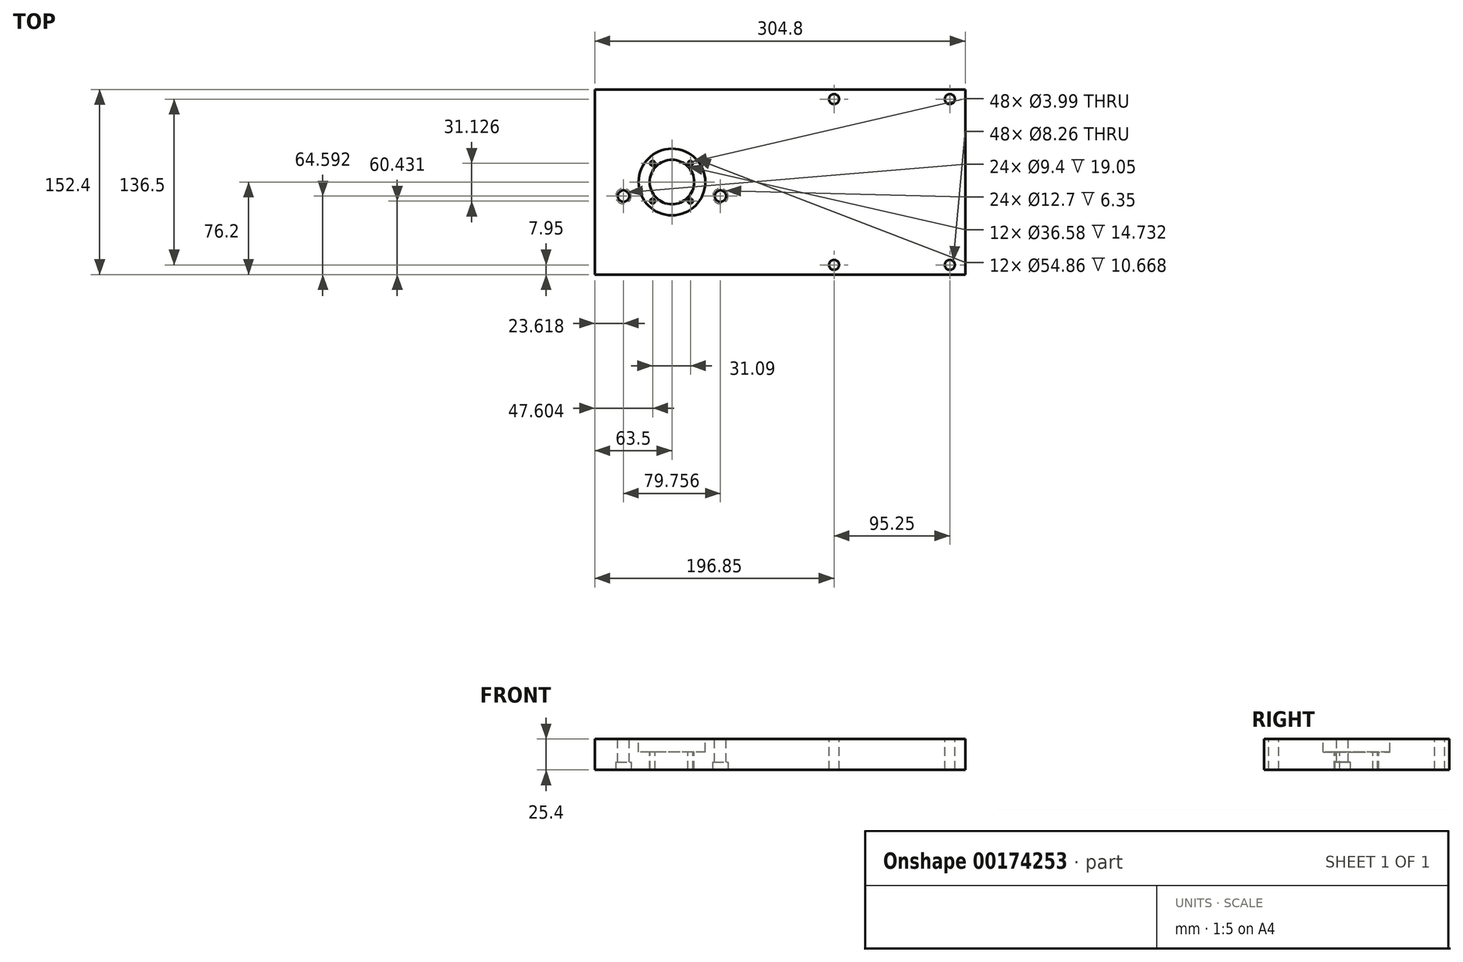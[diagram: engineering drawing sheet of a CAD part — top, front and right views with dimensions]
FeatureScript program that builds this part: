
annotation { "Feature Type Name" : "Feature", "Feature Type Description" : "" }
export const myFeature = defineFeature(function(context is Context, id is Id, definition is map)
    precondition{}
    {
        {
            var Q0;
            Q0=qCreatedBy(makeId("Top.planeOp"),FACE);
            var sketch = newSketch(context, id + "F0", { "sketchPlane" : qUnion([Q0])});
            skLineSegment(sketch, "E0.bottom", {"start": v(-152.4, 76.2) * mm, "end": v(152.4, 76.2) * mm});
            skLineSegment(sketch, "E0.top", {"start": v(-152.4, -76.2) * mm, "end": v(152.4, -76.2) * mm});
            skLineSegment(sketch, "E0.left", {"start": v(-152.4, 76.2) * mm, "end": v(-152.4, -76.2) * mm});
            skLineSegment(sketch, "E0.right", {"start": v(152.4, 76.2) * mm, "end": v(152.4, -76.2) * mm});
            skPoint(sketch, "E0.middle", {"position": v(0, 0) * mm});
            skSolve(sketch);
        }
        {
            var Q0;
            Q0=qSketchRegion(id+"F0",true);
            extrude(context, id + "F1", {"entities" : qUnion([Q0]), "oppositeDirection" : true, "depth" : 25.4 * mm});
        }
        {
            var Q0;
            Q0=makeQuery(id+"F1.opExtrude","CAP_FACE",FACE,{"disambiguationData":[OSD([sQuery(id+"F0.wireOp",EDGE,"E0.bottom"),sQuery(id+"F0.wireOp",EDGE,"E0.top"),sQuery(id+"F0.wireOp",EDGE,"E0.left"),sQuery(id+"F0.wireOp",EDGE,"E0.right")])],"isStart":true});
            var sketch = newSketch(context, id + "F2", { "sketchPlane" : qUnion([Q0])});
            skCircle(sketch, "E1", {"center": v(-88.9, 0) * mm, "radius": 18.29 * mm});
            skSolve(sketch);
        }
        {
            var Q0;
            Q0=qSketchRegion(id+"F2",true);
            extrude(context, id + "F3", {"entities" : qUnion([Q0]), "operationType" : NewBodyOperationType.REMOVE, "endBound" : BoundingType.THROUGH_ALL, "oppositeDirection" : true, "depth" : 25.4 * mm});
        }
        {
            var Q0;
            Q0=makeQuery(id+"F1.opExtrude","CAP_FACE",FACE,{"disambiguationData":[OSD([sQuery(id+"F0.wireOp",EDGE,"E0.bottom"),sQuery(id+"F0.wireOp",EDGE,"E0.top"),sQuery(id+"F0.wireOp",EDGE,"E0.left"),sQuery(id+"F0.wireOp",EDGE,"E0.right")])],"isStart":true});
            var sketch = newSketch(context, id + "F4", { "sketchPlane" : qUnion([Q0])});
            skCircle(sketch, "E2", {"center": v(-88.9, 0) * mm, "radius": 27.43 * mm});
            skSolve(sketch);
        }
        {
            var Q0;
            Q0=qSketchRegion(id+"F4",true);
            extrude(context, id + "F5", {"entities" : qUnion([Q0]), "operationType" : NewBodyOperationType.REMOVE, "oppositeDirection" : true, "depth" : 10.67 * mm});
        }
        {
            var Q0;
            Q0=makeQuery(id+"F5.boolean.opBoolean","COPY",FACE,{"derivedFrom":makeQuery(id+"F5.opExtrude","CAP_FACE",FACE,{"disambiguationData":[OSD([sQuery(id+"F4.wireOp",EDGE,"E2")])],"isStart":false})});
            var sketch = newSketch(context, id + "F6", { "sketchPlane" : qUnion([Q0])});
            skCircle(sketch, "E3", {"center": v(-104.8, 15.36) * mm, "radius": 2 * mm});
            skCircle(sketch, "E4", {"center": v(-73.7, 15.36) * mm, "radius": 2 * mm});
            skCircle(sketch, "E5", {"center": v(-73.7, -15.77) * mm, "radius": 2 * mm});
            skCircle(sketch, "E6", {"center": v(-104.8, -15.77) * mm, "radius": 2 * mm});
            skSolve(sketch);
        }
        {
            var Q0;
            Q0=sQuery(id+"F6.wireOp",VERTEX,"E3.center");
            var Q1;
            Q1=sQuery(id+"F6.wireOp",VERTEX,"E6.center");
            var Q2;
            Q2=sQuery(id+"F6.wireOp",VERTEX,"E5.center");
            var Q3;
            Q3=sQuery(id+"F6.wireOp",VERTEX,"E4.center");
            var Q4;
            Q4=makeQuery(id+"F1.opExtrude","SWEPT_BODY",BODY,{"disambiguationData":[OSD([sQuery(id+"F0.wireOp",EDGE,"E0.bottom"),sQuery(id+"F0.wireOp",EDGE,"E0.top"),sQuery(id+"F0.wireOp",EDGE,"E0.left"),sQuery(id+"F0.wireOp",EDGE,"E0.right")])]});
            hole(context, id + "F7", {"style" : HoleStyle.SIMPLE, "endStyle" : HoleEndStyle.THROUGH, "holeDiameter" : 4 * mm, "locations" : qUnion([Q0, Q1, Q2, Q3]), "scope" : qUnion([Q4]), "isTappedThrough" : true});
        }
        {
            var Q0;
            Q0=makeQuery(id+"F1.opExtrude","CAP_FACE",FACE,{"disambiguationData":[OSD([sQuery(id+"F0.wireOp",EDGE,"E0.bottom"),sQuery(id+"F0.wireOp",EDGE,"E0.top"),sQuery(id+"F0.wireOp",EDGE,"E0.left"),sQuery(id+"F0.wireOp",EDGE,"E0.right")])],"isStart":true});
            var sketch = newSketch(context, id + "F8", { "sketchPlane" : qUnion([Q0])});
            skCircle(sketch, "E7", {"center": v(-49.03, -11.6) * mm, "radius": 4.7 * mm});
            skCircle(sketch, "E8", {"center": v(-128.78, -11.6) * mm, "radius": 4.7 * mm});
            skSolve(sketch);
        }
        {
            var Q0;
            Q0=makeQuery(id+"F8.imprint","IMPRINT",FACE,{"disambiguationData":[TD([[makeQuery(id+"F8.imprint","IMPRINT",EDGE,{"derivedFrom":sQuery(id+"F8.wireOp",EDGE,"E8")}),1.0]])]});
            var Q1;
            Q1=makeQuery(id+"F8.imprint","IMPRINT",FACE,{"disambiguationData":[TD([[makeQuery(id+"F8.imprint","IMPRINT",EDGE,{"derivedFrom":sQuery(id+"F8.wireOp",EDGE,"E7")}),1.0]])]});
            var Q2;
            Q2=sQuery(id+"F8.wireOp",EDGE,"E8");
            var Q3;
            Q3=sQuery(id+"F8.wireOp",EDGE,"E7");
            extrude(context, id + "F9", {"entities" : qUnion([Q0, Q1]), "operationType" : NewBodyOperationType.REMOVE, "surfaceEntities" : qUnion([Q2, Q3]), "endBound" : BoundingType.THROUGH_ALL, "oppositeDirection" : true, "depth" : 25.4 * mm});
        }
        {
            var Q0;
            Q0=makeQuery(id+"F1.opExtrude","CAP_FACE",FACE,{"disambiguationData":[OSD([sQuery(id+"F0.wireOp",EDGE,"E0.bottom"),sQuery(id+"F0.wireOp",EDGE,"E0.top"),sQuery(id+"F0.wireOp",EDGE,"E0.left"),sQuery(id+"F0.wireOp",EDGE,"E0.right")])],"isStart":false});
            var sketch = newSketch(context, id + "F10", { "sketchPlane" : qUnion([Q0])});
            skCircle(sketch, "E9", {"center": v(-128.78, 11.6) * mm, "radius": 6.35 * mm});
            skCircle(sketch, "E10", {"center": v(-49.03, 11.6) * mm, "radius": 6.35 * mm});
            skSolve(sketch);
        }
        {
            var Q0;
            Q0=qSketchRegion(id+"F10",true);
            extrude(context, id + "F11", {"entities" : qUnion([Q0]), "operationType" : NewBodyOperationType.REMOVE, "oppositeDirection" : true, "depth" : 6.35 * mm});
        }
        {
            var Q0;
            Q0=makeQuery(id+"F1.opExtrude","CAP_FACE",FACE,{"disambiguationData":[OSD([sQuery(id+"F0.wireOp",EDGE,"E0.bottom"),sQuery(id+"F0.wireOp",EDGE,"E0.top"),sQuery(id+"F0.wireOp",EDGE,"E0.left"),sQuery(id+"F0.wireOp",EDGE,"E0.right")])],"isStart":true});
            var sketch = newSketch(context, id + "F12", { "sketchPlane" : qUnion([Q0])});
            skCircle(sketch, "E11", {"center": v(44.45, 68.25) * mm, "radius": 4.13 * mm});
            skCircle(sketch, "E12", {"center": v(139.7, 68.25) * mm, "radius": 4.13 * mm});
            skCircle(sketch, "E13", {"center": v(44.45, -68.25) * mm, "radius": 4.13 * mm});
            skCircle(sketch, "E14", {"center": v(139.7, -68.25) * mm, "radius": 4.13 * mm});
            skSolve(sketch);
        }
        {
            var Q0;
            Q0=qSketchRegion(id+"F12",true);
            extrude(context, id + "F13", {"entities" : qUnion([Q0]), "operationType" : NewBodyOperationType.REMOVE, "endBound" : BoundingType.THROUGH_ALL, "oppositeDirection" : true, "depth" : 25.4 * mm});
        }
    });
